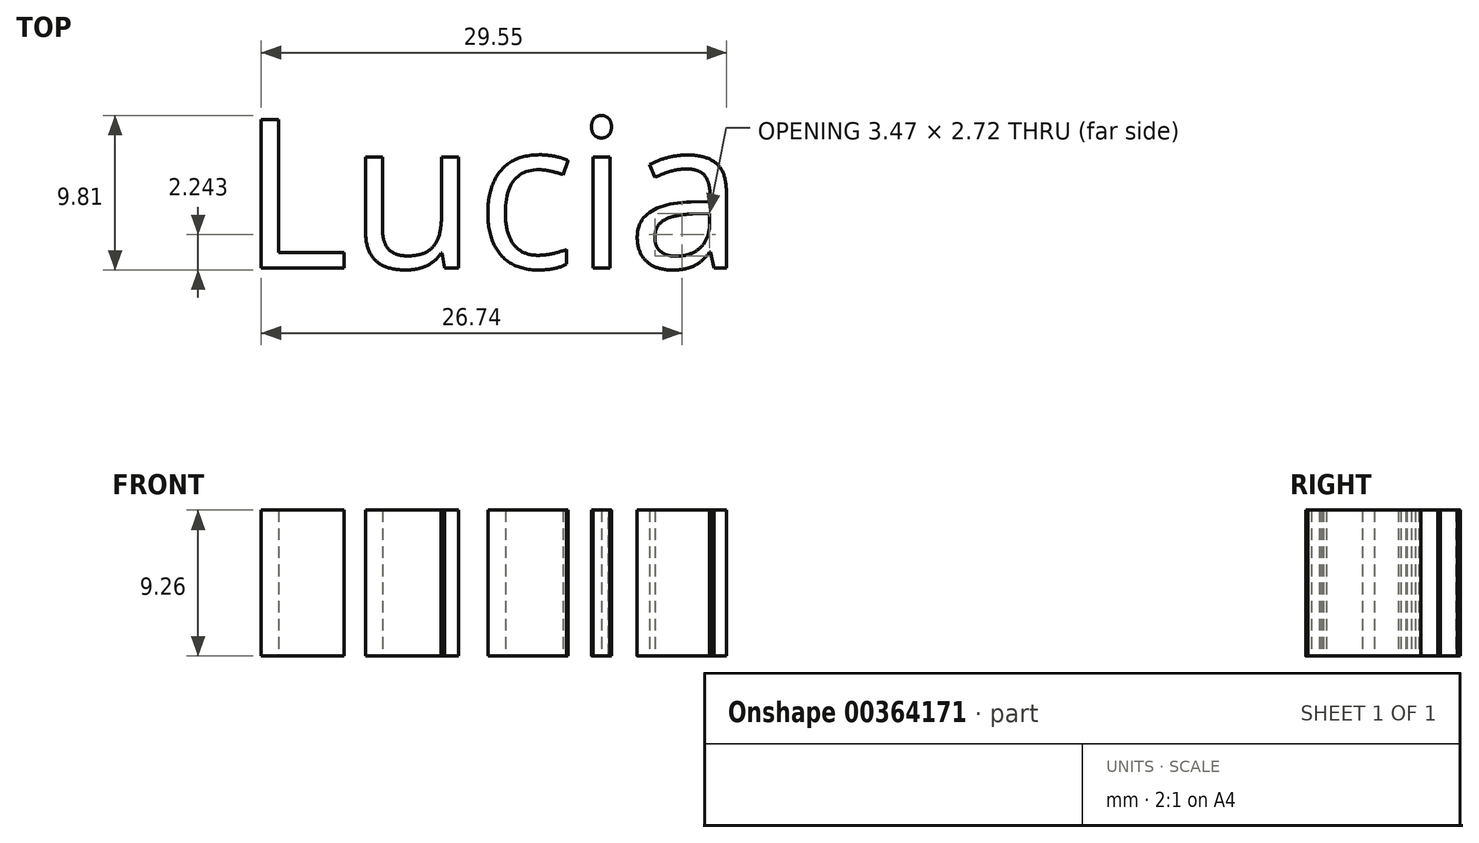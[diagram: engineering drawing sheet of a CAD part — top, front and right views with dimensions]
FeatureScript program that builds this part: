
annotation { "Feature Type Name" : "Feature", "Feature Type Description" : "" }
export const myFeature = defineFeature(function(context is Context, id is Id, definition is map)
    precondition{}
    {
        {
            var Q0;
            Q0=qCreatedBy(makeId("Top.planeOp"),FACE);
            var sketch = newSketch(context, id + "F0", { "sketchPlane" : qUnion([Q0])});
            skText(sketch, "E0", { "text": "Lucia", "fontName": "OpenSans-Regular.ttf"});
            const initialGuessF0  = {"E0": [-0.05462, -0.03776, 1, 0, 0.0095]};
            skSetInitialGuess(sketch, initialGuessF0);
            skSolve(sketch);
        }
        {
            var Q0;
            Q0 = qSketchRegion(id + "F0", true);
            extrude(context, id + "F1", {"entities" : qUnion([Q0]), "depth" : 9.26 * mm});
        }
    });
